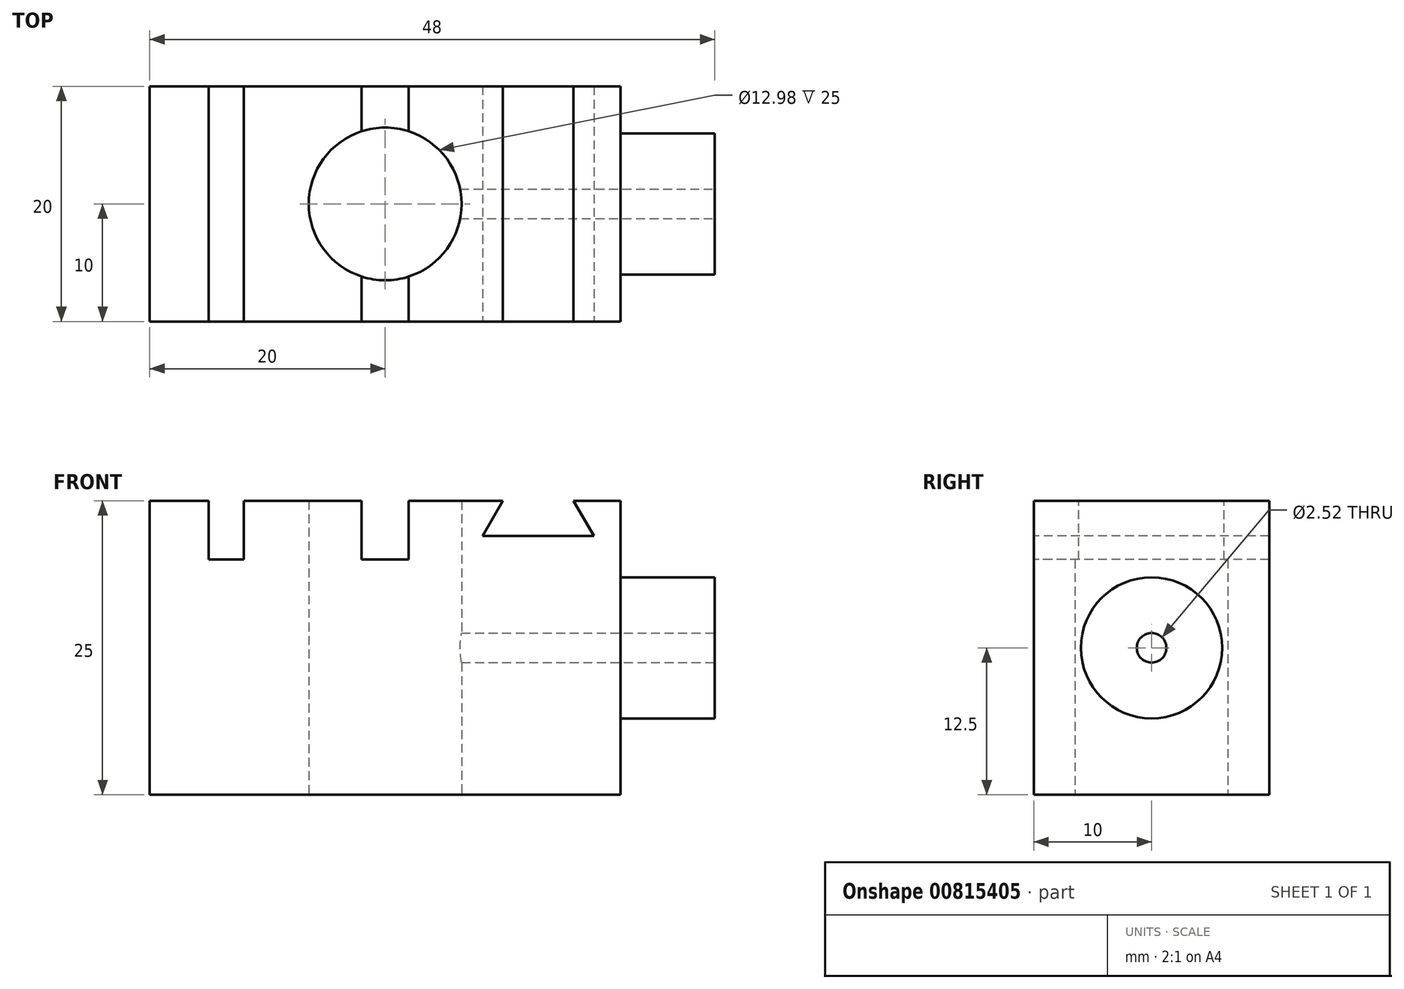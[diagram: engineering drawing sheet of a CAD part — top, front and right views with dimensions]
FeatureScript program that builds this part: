
annotation { "Feature Type Name" : "Feature", "Feature Type Description" : "" }
export const myFeature = defineFeature(function(context is Context, id is Id, definition is map)
    precondition{}
    {
        {
            var Q0;
            Q0=qCreatedBy(makeId("Top.planeOp"),FACE);
            var sketch = newSketch(context, id + "F0", { "sketchPlane" : qUnion([Q0])});
            skLineSegment(sketch, "E0.bottom", {"start": v(20, -10) * mm, "end": v(-20, -10) * mm});
            skLineSegment(sketch, "E0.top", {"start": v(20, 10) * mm, "end": v(-20, 10) * mm});
            skLineSegment(sketch, "E0.left", {"start": v(20, -10) * mm, "end": v(20, 10) * mm});
            skLineSegment(sketch, "E0.right", {"start": v(-20, -10) * mm, "end": v(-20, 10) * mm});
            skPoint(sketch, "E0.middle", {"position": v(0, 0) * mm});
            skCircle(sketch, "E1", {"center": v(0, 0) * mm, "radius": 6.5 * mm});
            skSolve(sketch);
        }
        {
            var Q0;
            Q0=makeQuery(id+"F0.imprint","IMPRINT",FACE,{"disambiguationData":[TD([[makeQuery(id+"F0.imprint","IMPRINT",EDGE,{"derivedFrom":sQuery(id+"F0.wireOp",EDGE,"E0.bottom")}),-1.0]])]});
            extrude(context, id + "F1", {"entities" : qUnion([Q0]), "depth" : 25 * mm, "offsetDistance" : 25 * mm});
        }
        {
            var Q0;
            Q0=makeQuery(id+"F1.opExtrude","CAP_FACE",FACE,{"disambiguationData":[OSD([sQuery(id+"F0.wireOp",EDGE,"E0.bottom"),sQuery(id+"F0.wireOp",EDGE,"E0.top"),sQuery(id+"F0.wireOp",EDGE,"E0.left"),sQuery(id+"F0.wireOp",EDGE,"E0.right"),sQuery(id+"F0.wireOp",EDGE,"E1")])],"isStart":false});
            var sketch = newSketch(context, id + "F2", { "sketchPlane" : qUnion([Q0])});
            skLineSegment(sketch, "E2.bottom", {"start": v(-15, 10) * mm, "end": v(-12, 10) * mm});
            skLineSegment(sketch, "E2.top", {"start": v(-15, -10) * mm, "end": v(-12, -10) * mm});
            skLineSegment(sketch, "E2.left", {"start": v(-15, 10) * mm, "end": v(-15, -10) * mm});
            skLineSegment(sketch, "E2.right", {"start": v(-12, 10) * mm, "end": v(-12, -10) * mm});
            skLineSegment(sketch, "E3", {"start": v(-2, 10) * mm, "end": v(-2, -10) * mm});
            skLineSegment(sketch, "E4", {"start": v(-2, -10) * mm, "end": v(2, -10) * mm});
            skLineSegment(sketch, "E5", {"start": v(2, -10) * mm, "end": v(2, 10) * mm});
            skLineSegment(sketch, "E6", {"start": v(2, 10) * mm, "end": v(-2, 10) * mm});
            skPoint(sketch, "E7", {"position": v(0, 0) * mm});
            skLineSegment(sketch, "E8", {"start": v(0, 10) * mm, "end": v(0, -10) * mm, "construction": true});
            skSolve(sketch);
        }
        {
            var Q0;
            Q0=makeQuery(id+"F2.imprint","IMPRINT",FACE,{"disambiguationData":[TD([[makeQuery(id+"F2.imprint","IMPRINT",EDGE,{"derivedFrom":sQuery(id+"F2.wireOp",EDGE,"E2.bottom")}),1.0]])]});
            var Q1;
            {var subQ0=sQuery(id+"F2.wireOp",EDGE,"E6");Q1=makeQuery(id+"F2.imprint","IMPRINT",FACE,{"disambiguationData":[TD([[makeQuery(id+"F2.imprint","IMPRINT",EDGE,{"derivedFrom":subQ0}),1.0]])]});}
            var Q2;
            {var subQ0=sQuery(id+"F2.wireOp",EDGE,"E4");Q2=makeQuery(id+"F2.imprint","IMPRINT",FACE,{"disambiguationData":[TD([[makeQuery(id+"F2.imprint","IMPRINT",EDGE,{"derivedFrom":subQ0}),-1.0]])]});}
            extrude(context, id + "F3", {"entities" : qUnion([Q0, Q1, Q2]), "operationType" : NewBodyOperationType.REMOVE, "oppositeDirection" : true, "depth" : 5 * mm, "offsetDistance" : 25 * mm});
        }
        {
            var Q0;
            Q0=makeQuery(id+"F1.opExtrude","SWEPT_FACE",FACE,{"disambiguationData":[OSD([sQuery(id+"F0.wireOp",EDGE,"E0.bottom")])]});
            var sketch = newSketch(context, id + "F4", { "sketchPlane" : qUnion([Q0])});
            skLineSegment(sketch, "E9", {"start": v(10, 25) * mm, "end": v(8.27, 22) * mm});
            skLineSegment(sketch, "E10", {"start": v(8.27, 22) * mm, "end": v(17.73, 22) * mm});
            skLineSegment(sketch, "E11", {"start": v(17.73, 22) * mm, "end": v(16, 25) * mm});
            skLineSegment(sketch, "E12", {"start": v(16, 25) * mm, "end": v(10, 25) * mm});
            skLineSegment(sketch, "E13", {"start": v(13, 22) * mm, "end": v(13, 25) * mm, "construction": true});
            skSolve(sketch);
        }
        {
            var Q0;
            Q0=makeQuery(id+"F4.imprint","IMPRINT",FACE,{"disambiguationData":[TD([[makeQuery(id+"F4.imprint","IMPRINT",EDGE,{"derivedFrom":sQuery(id+"F4.wireOp",EDGE,"E9")}),1.0]])]});
            extrude(context, id + "F5", {"entities" : qUnion([Q0]), "operationType" : NewBodyOperationType.REMOVE, "endBound" : BoundingType.THROUGH_ALL, "oppositeDirection" : true, "depth" : 25 * mm, "offsetDistance" : 25 * mm});
        }
        {
            var Q0;
            Q0=makeQuery(id+"F1.opExtrude","SWEPT_FACE",FACE,{"disambiguationData":[OSD([sQuery(id+"F0.wireOp",EDGE,"E0.left")])]});
            var sketch = newSketch(context, id + "F6", { "sketchPlane" : qUnion([Q0])});
            skCircle(sketch, "E14", {"center": v(0, 12.5) * mm, "radius": 6 * mm});
            skPoint(sketch, "E14.centerSnap0", {"position": v(-10, 12.5) * mm});
            skPoint(sketch, "E14.centerSnap1", {"position": v(0, 25) * mm});
            skSolve(sketch);
        }
        {
            var Q0;
            Q0=makeQuery(id+"F6.imprint","IMPRINT",FACE,{"disambiguationData":[TD([[makeQuery(id+"F6.imprint","IMPRINT",EDGE,{"derivedFrom":sQuery(id+"F6.wireOp",EDGE,"E14")}),1.0]])]});
            extrude(context, id + "F7", {"entities" : qUnion([Q0]), "operationType" : NewBodyOperationType.ADD, "depth" : 8 * mm, "offsetDistance" : 25 * mm});
        }
        {
            var Q0;
            Q0=makeQuery(id+"F7.opExtrude","CAP_FACE",FACE,{"disambiguationData":[OSD([sQuery(id+"F6.wireOp",EDGE,"E14")])],"isStart":false});
            var sketch = newSketch(context, id + "F8", { "sketchPlane" : qUnion([Q0])});
            skCircle(sketch, "E15", {"center": v(0, 12.5) * mm, "radius": 1.26 * mm});
            skSolve(sketch);
        }
        {
            var Q0;
            Q0=makeQuery(id+"F8.imprint","IMPRINT",FACE,{"disambiguationData":[TD([[makeQuery(id+"F8.imprint","IMPRINT",EDGE,{"derivedFrom":sQuery(id+"F8.wireOp",EDGE,"E15")}),1.0]])]});
            extrude(context, id + "F9", {"entities" : qUnion([Q0]), "operationType" : NewBodyOperationType.REMOVE, "oppositeDirection" : true, "depth" : 25 * mm, "offsetDistance" : 25 * mm});
        }
    });
